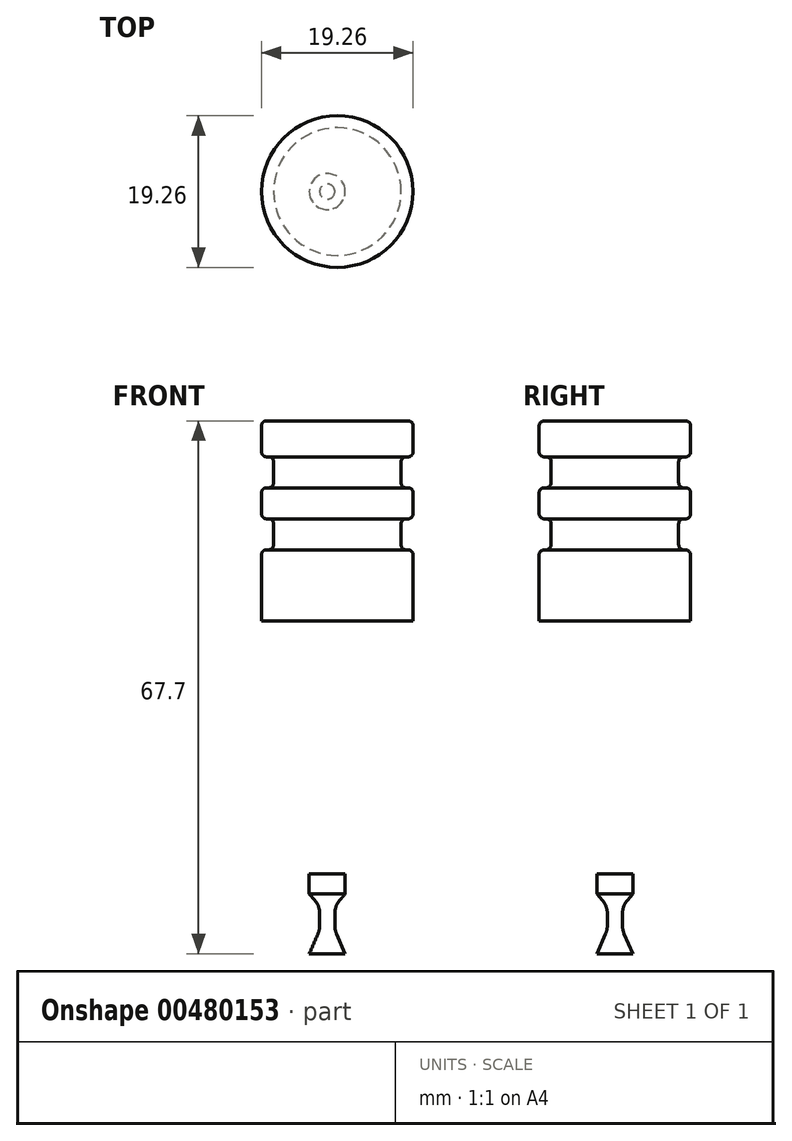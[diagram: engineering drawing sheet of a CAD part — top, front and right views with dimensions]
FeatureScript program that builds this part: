
annotation { "Feature Type Name" : "Feature", "Feature Type Description" : "" }
export const myFeature = defineFeature(function(context is Context, id is Id, definition is map)
    precondition{}
    {
        {
            var Q0;
            Q0=qCreatedBy(makeId("Front.planeOp"),FACE);
            var sketch = newSketch(context, id + "F0", { "sketchPlane" : qUnion([Q0])});
            skLineSegment(sketch, "E0", {"start": v(0, 0) * mm, "end": v(0, 25.4) * mm});
            skLineSegment(sketch, "E1", {"start": v(0, 25.4) * mm, "end": v(9, 25.4) * mm});
            skLineSegment(sketch, "E2", {"start": v(9.63, 24.77) * mm, "end": v(9.63, 21.46) * mm});
            skLineSegment(sketch, "E3", {"start": v(9, 20.83) * mm, "end": v(8.74, 20.83) * mm});
            skLineSegment(sketch, "E4", {"start": v(8.1, 20.2) * mm, "end": v(8.1, 17.53) * mm});
            skLineSegment(sketch, "E5", {"start": v(8.74, 16.9) * mm, "end": v(9, 16.9) * mm});
            skLineSegment(sketch, "E6", {"start": v(9.63, 16.26) * mm, "end": v(9.63, 13.59) * mm});
            skLineSegment(sketch, "E7", {"start": v(9, 12.95) * mm, "end": v(8.74, 12.95) * mm});
            skLineSegment(sketch, "E8", {"start": v(8.1, 12.32) * mm, "end": v(8.1, 9.65) * mm});
            skLineSegment(sketch, "E9", {"start": v(8.74, 9.02) * mm, "end": v(9, 9.02) * mm});
            skLineSegment(sketch, "E10", {"start": v(9.63, 8.38) * mm, "end": v(9.63, 0) * mm});
            skLineSegment(sketch, "E11", {"start": v(9.63, 0) * mm, "end": v(0, 0) * mm});
            skPoint(sketch, "E12.visualSharp", {"position": v(9.63, 25.4) * mm});
            skArc(sketch, "E12.filletArc", {"start": v(9.63, 24.77) * mm, "mid": v(9.44, 25.21) * mm, "end": v(9, 25.4) * mm});
            skPoint(sketch, "E13.visualSharp", {"position": v(9.63, 20.83) * mm});
            skArc(sketch, "E13.filletArc", {"start": v(9, 20.83) * mm, "mid": v(9.44, 21.01) * mm, "end": v(9.63, 21.46) * mm});
            skPoint(sketch, "E14.visualSharp", {"position": v(8.1, 16.9) * mm});
            skArc(sketch, "E14.filletArc", {"start": v(8.1, 17.53) * mm, "mid": v(8.29, 17.08) * mm, "end": v(8.74, 16.9) * mm});
            skPoint(sketch, "E15.visualSharp", {"position": v(8.1, 20.83) * mm});
            skArc(sketch, "E15.filletArc", {"start": v(8.74, 20.83) * mm, "mid": v(8.29, 20.64) * mm, "end": v(8.1, 20.2) * mm});
            skPoint(sketch, "E16.visualSharp", {"position": v(9.63, 16.9) * mm});
            skArc(sketch, "E16.filletArc", {"start": v(9.63, 16.26) * mm, "mid": v(9.44, 16.7) * mm, "end": v(9, 16.9) * mm});
            skPoint(sketch, "E17.visualSharp", {"position": v(9.63, 12.95) * mm});
            skArc(sketch, "E17.filletArc", {"start": v(9, 12.95) * mm, "mid": v(9.44, 13.14) * mm, "end": v(9.63, 13.59) * mm});
            skPoint(sketch, "E18.visualSharp", {"position": v(8.1, 12.95) * mm});
            skArc(sketch, "E18.filletArc", {"start": v(8.74, 12.95) * mm, "mid": v(8.29, 12.77) * mm, "end": v(8.1, 12.32) * mm});
            skPoint(sketch, "E19.visualSharp", {"position": v(8.1, 9.02) * mm});
            skArc(sketch, "E19.filletArc", {"start": v(8.1, 9.65) * mm, "mid": v(8.29, 9.2) * mm, "end": v(8.74, 9.02) * mm});
            skPoint(sketch, "E20.visualSharp", {"position": v(9.63, 9.02) * mm});
            skArc(sketch, "E20.filletArc", {"start": v(9.63, 8.38) * mm, "mid": v(9.44, 8.83) * mm, "end": v(9, 9.02) * mm});
            skSolve(sketch);
        }
        {
            var Q0;
            Q0=makeQuery(id+"F0.imprint","IMPRINT",FACE,{"disambiguationData":[TD([[makeQuery(id+"F0.imprint","IMPRINT",EDGE,{"derivedFrom":sQuery(id+"F0.wireOp",EDGE,"E0")}),-1.0]])]});
            var Q1;
            Q1=sQuery(id+"F0.wireOp",EDGE,"E0");
            revolve(context, id + "F1", {"entities" : qUnion([Q0]), "axis" : qUnion([Q1]), "revolveType" : RevolveType.FULL});
        }
        {
            var Q0;
            Q0=qCreatedBy(makeId("Front.planeOp"),FACE);
            var sketch = newSketch(context, id + "F2", { "sketchPlane" : qUnion([Q0])});
            skLineSegment(sketch, "E21", {"start": v(-1.28, -32.14) * mm, "end": v(1, -32.14) * mm});
            skLineSegment(sketch, "E22", {"start": v(1, -32.14) * mm, "end": v(1, -34.68) * mm});
            skLineSegment(sketch, "E23", {"start": v(1, -34.68) * mm, "end": v(-0.31, -36.23) * mm});
            skLineSegment(sketch, "E24", {"start": v(-0.31, -36.23) * mm, "end": v(-0.31, -39.27) * mm});
            skLineSegment(sketch, "E25", {"start": v(-0.31, -39.27) * mm, "end": v(1, -42.3) * mm});
            skLineSegment(sketch, "E26", {"start": v(1, -42.3) * mm, "end": v(-1.28, -42.3) * mm});
            skLineSegment(sketch, "E27", {"start": v(-1.28, -42.3) * mm, "end": v(-1.28, -32.14) * mm});
            skSolve(sketch);
        }
        {
            var Q0;
            Q0=makeQuery(id+"F2.imprint","IMPRINT",FACE,{"disambiguationData":[TD([[makeQuery(id+"F2.imprint","IMPRINT",EDGE,{"derivedFrom":sQuery(id+"F2.wireOp",EDGE,"E21")}),-1.0]])]});
            var Q1;
            Q1=sQuery(id+"F2.wireOp",EDGE,"E27");
            revolve(context, id + "F3", {"entities" : qUnion([Q0]), "axis" : qUnion([Q1]), "revolveType" : RevolveType.FULL});
        }
        {
            var Q0;
            Q0=makeQuery(id+"F3.opRevolve","SWEPT_FACE",FACE,{"disambiguationData":[OSD([sQuery(id+"F2.wireOp",EDGE,"E24")])]});
            fillet(context, id + "F4", {"entities" : qUnion([Q0]), "radius" : 2.54 * mm, "tangentPropagation" : true, "allowEdgeOverflow" : false});
        }
    });
